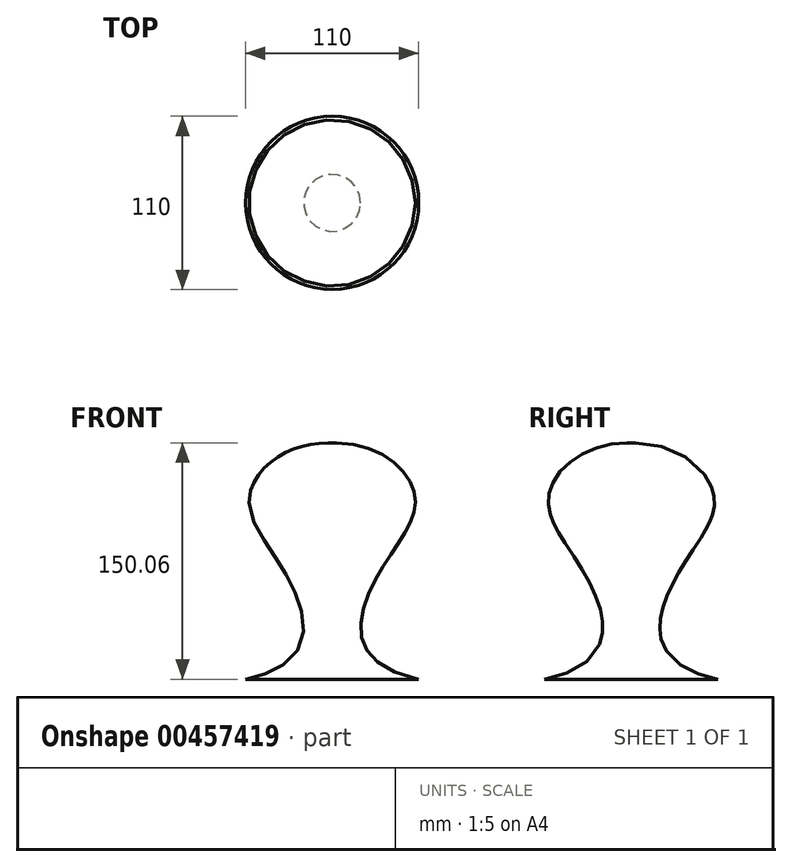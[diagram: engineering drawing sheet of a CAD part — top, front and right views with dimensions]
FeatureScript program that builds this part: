
annotation { "Feature Type Name" : "Feature", "Feature Type Description" : "" }
export const myFeature = defineFeature(function(context is Context, id is Id, definition is map)
    precondition{}
    {
        {
            var Q0;
            Q0=qCreatedBy(makeId("Front.planeOp"),FACE);
            var sketch = newSketch(context, id + "F0", { "sketchPlane" : qUnion([Q0])});
            skLineSegment(sketch, "E0", {"start": v(0, 0) * mm, "end": v(0, 150) * mm});
            skLineSegment(sketch, "E1", {"start": v(0, 0) * mm, "end": v(55, 0) * mm});
            skFitSpline(sketch, "E2", {"points": [v(55, 0) * mm, v(28.3, 64.58) * mm, v(52.63, 116) * mm, v(0, 150) * mm, v(-70.74, 69.15) * mm], "startDerivative": vector(-596.22, 124.66) * mm, "endDerivative": vector(210.88, -436.1) * mm});
            skSolve(sketch);
        }
        {
            var Q0;
            Q0=makeQuery(id+"F0.imprint","IMPRINT",FACE,{"disambiguationData":[TD([[makeQuery(id+"F0.imprint","IMPRINT",EDGE,{"derivedFrom":sQuery(id+"F0.wireOp",EDGE,"E0")}),-1.0]])]});
            var Q1;
            Q1=sQuery(id+"F0.wireOp",EDGE,"E0");
            revolve(context, id + "F1", {"surfaceOperationType" : NewSurfaceOperationType.NEW, "entities" : qUnion([Q0]), "axis" : qUnion([Q1]), "revolveType" : RevolveType.FULL});
        }
    });
